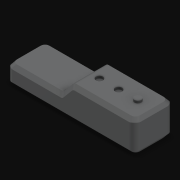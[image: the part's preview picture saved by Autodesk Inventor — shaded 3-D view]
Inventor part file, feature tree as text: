
AUTODESK INVENTOR PART (.ipt)
format: ipt  version: 2021 (Build 250183000, 183)  size: 265,216 bytes
history: native  units: in
note: dims shown in document units (in); Inventor stores cm internally (conversion verified against a paired STEP export)
features: chamfer x12, extrude x4, sketch x4, fillet x2
ambient origin geometry x8: Origin, YZ Plane, XZ Plane, XY Plane, X Axis, Y Axis, Z Axis, Center Point
bodies: Solid1 (feature_tree)
feature tree (22):
  extrude  "Extrusion1"  Depth=0.827in
  extrude  "Extrusion2"  Depth=1.9283in
  chamfer  "Chamfer1"  [1 undecoded]
  chamfer  "Chamfer2"  Distance=0.8933in
  chamfer  "Chamfer3"  Distance=0.077in Angle=45.0deg
  chamfer  "Chamfer4"  Distance=0.096in Angle=45.0deg
  chamfer  "Chamfer5"  Distance=0.096in Angle=45.0deg
  chamfer  "Chamfer6"  Distance=0.096in Angle=45.0deg
  chamfer  "Chamfer7"  Distance=0.096in Angle=45.0deg
  chamfer  "Chamfer8"  Distance=0.096in Angle=45.0deg
  chamfer  "Chamfer9"  Distance=0.096in Angle=45.0deg
  chamfer  "Chamfer10"  Distance=0.099in Angle=45.0deg
  chamfer  "Chamfer11"  Distance=0.099in Angle=45.0deg
  chamfer  "Chamfer12"  Distance=0.074in Angle=45.0deg
  fillet  "Fillet1"  Radius=0.074in
  fillet  "Fillet2"  Radius=0.07in
  sketch  "Sketch3"  dims[d6=0.492in]
  extrude  "Extrusion3"  Depth=0.098in
  extrude  "Extrusion4"  Depth=0.148in
  sketch  "Sketch1"  dims[d0=3.327in d1=0.827in]
  sketch  "Sketch2"  dims[d2=1.0in d3=0.0in d5=1.9283in]
  sketch  "Sketch6"  dims[d7=0.0in d8=0.0in d9=0.0in d10=0.8933in d11=0.077in d12=0.096in d13=45.0deg d14=0.096in d15=0.059in d16=45.0deg d17=0.096in d18=0.077in d19=45.0deg d20=0.096in d21=0.077in d22=45.0deg d23=0.096in d24=0.077in d25=45.0deg d26=0.096in d27=0.077in d28=45.0deg d29=0.096in d30=0.077in d31=45.0deg d32=0.099in d33=0.102in d34=45.0deg d35=0.099in d36=0.102in d37=45.0deg d38=0.074in d39=0.102in d40=45.0deg d41=0.074in d42=0.102in d43=45.0deg d44=0.07in d45=0.102in d46=45.0deg d47=0.098in d48=0.148in d50=0.418in d51=0.5in d52=0.18in d53=0.18in d54=0.5in d55=0.5in d56=0.5in d57=0.5in d73=0.0625in d74=0.0in d76=0.18in d77=0.5in d78=0.5in d79=0.0625in d80=0.0in]
note: 1 required parameter value undecoded (feature->parameter linkage not recoverable at this tier; creation-order binding heuristic only, values carry confidence <= 0.55)
